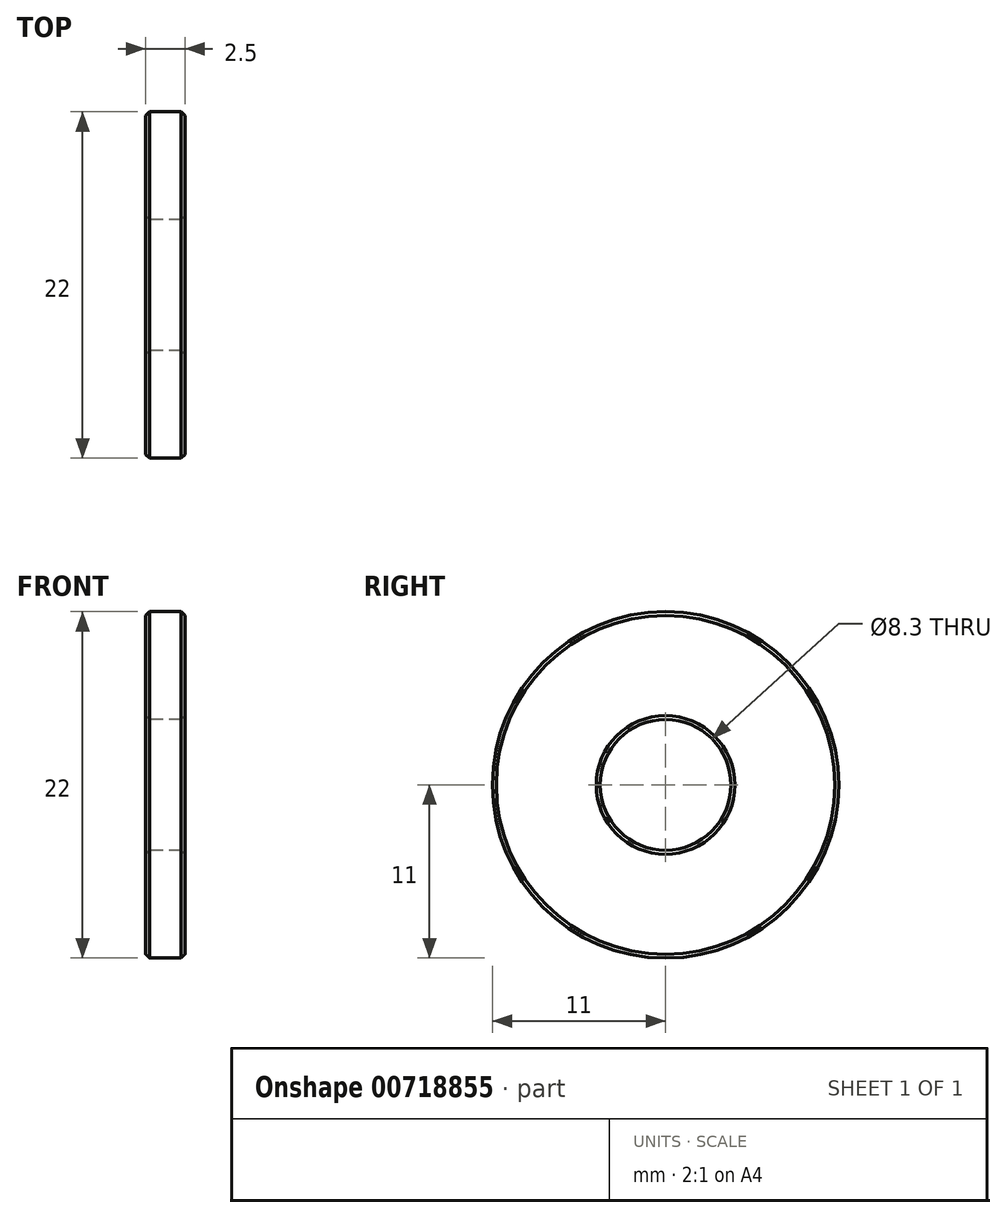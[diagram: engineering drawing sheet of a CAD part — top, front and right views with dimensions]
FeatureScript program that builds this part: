
annotation { "Feature Type Name" : "Feature", "Feature Type Description" : "" }
export const myFeature = defineFeature(function(context is Context, id is Id, definition is map)
    precondition{}
    {
        {
            var Q0;
            Q0=qCreatedBy(makeId("Right.planeOp"),FACE);
            var sketch = newSketch(context, id + "F0", { "sketchPlane" : qUnion([Q0])});
            skCircle(sketch, "E0", {"center": v(0, 0) * mm, "radius": 4.15 * mm});
            skCircle(sketch, "E1", {"center": v(0, 0) * mm, "radius": 11 * mm});
            skSolve(sketch);
        }
        {
            var Q0;
            Q0=makeQuery(id+"F0.imprint","IMPRINT",FACE,{"disambiguationData":[TD([[makeQuery(id+"F0.imprint","IMPRINT",EDGE,{"derivedFrom":sQuery(id+"F0.wireOp",EDGE,"E0")}),-1.0]])]});
            extrude(context, id + "F1", {"entities" : qUnion([Q0]), "depth" : 2.5 * mm, "offsetDistance" : 25 * mm});
        }
        {
            var Q0;
            Q0=makeQuery(id+"F1.opExtrude","CAP_EDGE",EDGE,{"disambiguationData":[OSD([sQuery(id+"F0.wireOp",EDGE,"E1")])],"isStart":false});
            var Q1;
            Q1=makeQuery(id+"F1.opExtrude","CAP_EDGE",EDGE,{"disambiguationData":[OSD([sQuery(id+"F0.wireOp",EDGE,"E0")])],"isStart":false});
            var Q2;
            Q2=makeQuery(id+"F1.opExtrude","CAP_EDGE",EDGE,{"disambiguationData":[OSD([sQuery(id+"F0.wireOp",EDGE,"E0")])],"isStart":true});
            var Q3;
            Q3=makeQuery(id+"F1.opExtrude","CAP_EDGE",EDGE,{"disambiguationData":[OSD([sQuery(id+"F0.wireOp",EDGE,"E1")])],"isStart":true});
            chamfer(context, id + "F2", {"entities" : qUnion([Q0, Q1, Q2, Q3]), "width" : 0.25 * mm, "tangentPropagation" : true});
        }
    });
